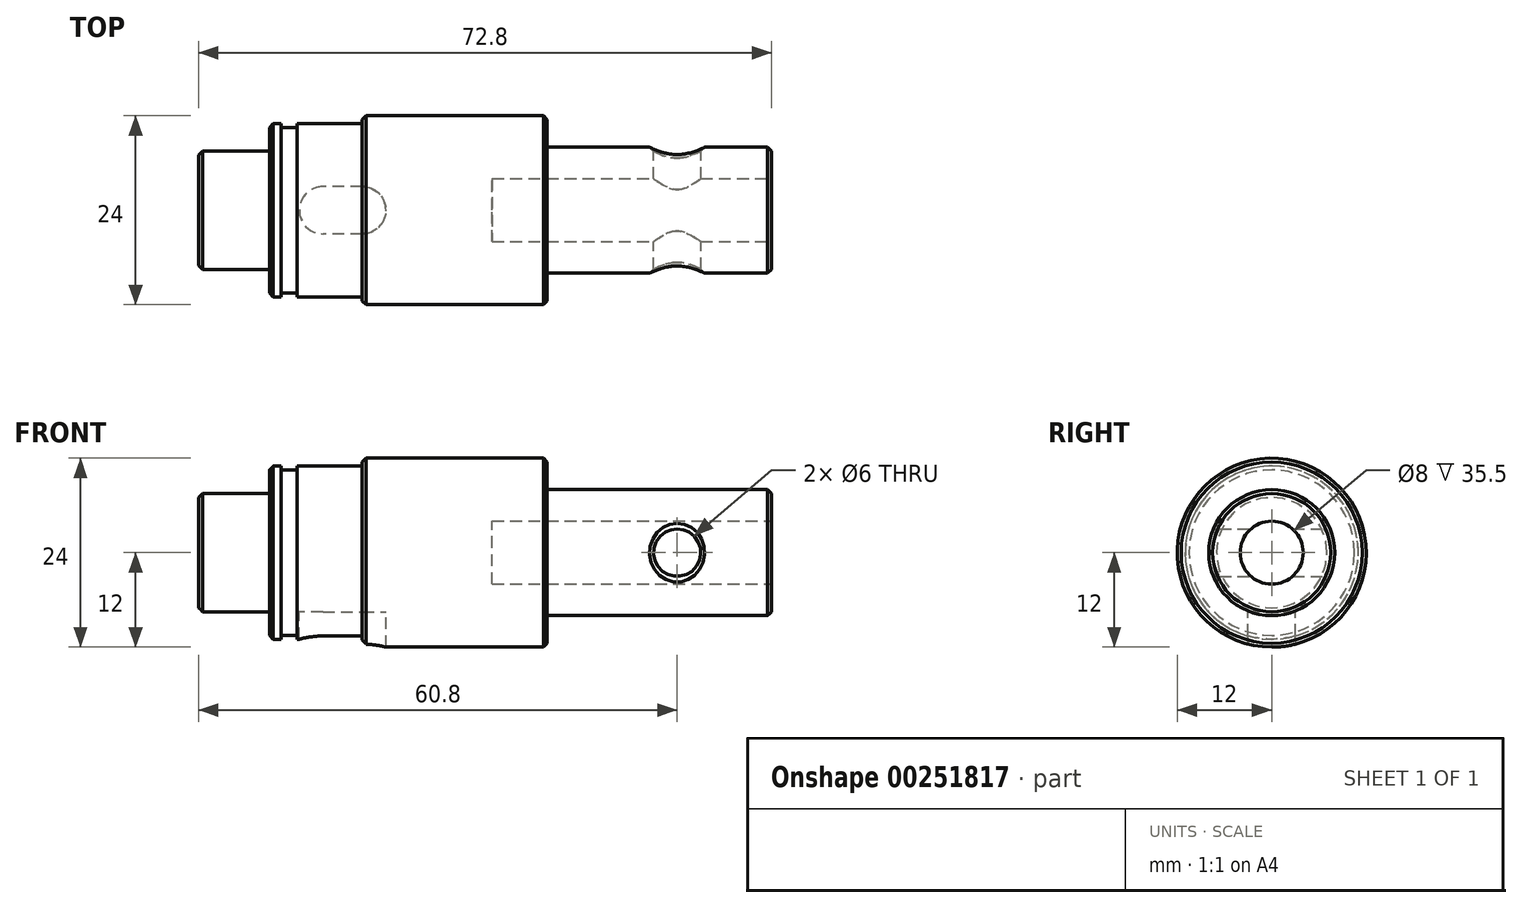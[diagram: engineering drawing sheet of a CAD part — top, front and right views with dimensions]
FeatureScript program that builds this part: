
annotation { "Feature Type Name" : "Feature", "Feature Type Description" : "" }
export const myFeature = defineFeature(function(context is Context, id is Id, definition is map)
    precondition{}
    {
        {
            var Q0;
            Q0=qCreatedBy(makeId("Front.planeOp"),FACE);
            var sketch = newSketch(context, id + "F0", { "sketchPlane" : qUnion([Q0])});
            skLineSegment(sketch, "E0", {"start": v(-50.69, 0) * mm, "end": v(53.02, 0) * mm});
            skLineSegment(sketch, "E1", {"start": v(0, 0) * mm, "end": v(0, 12) * mm});
            skLineSegment(sketch, "E2", {"start": v(0, 12) * mm, "end": v(23.5, 12) * mm});
            skLineSegment(sketch, "E3", {"start": v(23.5, 12) * mm, "end": v(23.5, 0) * mm});
            skLineSegment(sketch, "E4", {"start": v(0, 11) * mm, "end": v(-8.3, 11) * mm});
            skLineSegment(sketch, "E5", {"start": v(-8.3, 11) * mm, "end": v(-8.3, 0) * mm});
            skLineSegment(sketch, "E6", {"start": v(-8.3, 0) * mm, "end": v(0, 0) * mm});
            skLineSegment(sketch, "E7", {"start": v(-8.3, 10.5) * mm, "end": v(-10.3, 10.5) * mm});
            skLineSegment(sketch, "E8", {"start": v(-10.3, 11) * mm, "end": v(-10.3, 0) * mm});
            skLineSegment(sketch, "E9", {"start": v(-10.3, 0) * mm, "end": v(-11.8, 0) * mm});
            skLineSegment(sketch, "E10", {"start": v(-11.8, 0) * mm, "end": v(-11.8, 11) * mm});
            skLineSegment(sketch, "E11", {"start": v(-11.8, 11) * mm, "end": v(-10.3, 11) * mm});
            skLineSegment(sketch, "E12", {"start": v(-11.8, 7.5) * mm, "end": v(-20.8, 7.5) * mm});
            skLineSegment(sketch, "E13", {"start": v(-20.8, 7.5) * mm, "end": v(-20.8, 0) * mm});
            skLineSegment(sketch, "E14", {"start": v(23.5, 8) * mm, "end": v(52, 8) * mm});
            skLineSegment(sketch, "E15", {"start": v(52, 8) * mm, "end": v(52, 0) * mm});
            skSolve(sketch);
        }
        {
            var Q0;
            Q0 = qSketchRegion(id + "F0", true);
            var Q1;
            Q1=sQuery(id+"F0.wireOp",EDGE,"E0");
            revolve(context, id + "F1", {"entities" : qUnion([Q0]), "axis" : qUnion([Q1]), "revolveType" : RevolveType.FULL});
        }
        {
            var Q0;
            Q0=qCreatedBy(makeId("Top.planeOp"),FACE);
            cPlane(context, id + "F2", {"entities" : qUnion([Q0]), "cplaneType" : CPlaneType.OFFSET, "offset" : 7.5 * mm, "oppositeDirection" : true, "width" : 150 * mm, "height" : 150 * mm});
        }
        {
            var Q0;
            Q0=qCreatedBy(id+"F2.planeOp",FACE);
            var sketch = newSketch(context, id + "F3", { "sketchPlane" : qUnion([Q0])});
            skArc(sketch, "E16", {"start": v(0, -3) * mm, "mid": v(3, 0) * mm, "end": v(0, 3) * mm});
            skArc(sketch, "E17", {"start": v(-5, 3) * mm, "mid": v(-8, 0) * mm, "end": v(-5, -3) * mm});
            skLineSegment(sketch, "E18", {"start": v(-5, -2.48) * mm, "end": v(-5, 2.81) * mm, "construction": true});
            skLineSegment(sketch, "E19", {"start": v(0, -2.85) * mm, "end": v(0, 3.74) * mm, "construction": true});
            skLineSegment(sketch, "E20", {"start": v(-5, -3) * mm, "end": v(0, -3) * mm});
            skLineSegment(sketch, "E21", {"start": v(-5, 3) * mm, "end": v(0, 3) * mm});
            skSolve(sketch);
        }
        {
            var Q0;
            Q0 = qSketchRegion(id + "F3", true);
            extrude(context, id + "F4", {"entities" : qUnion([Q0]), "operationType" : NewBodyOperationType.REMOVE, "endBound" : BoundingType.THROUGH_ALL, "oppositeDirection" : true, "depth" : 25 * mm});
        }
        {
            var Q0;
            Q0=qCreatedBy(makeId("Front.planeOp"),FACE);
            var sketch = newSketch(context, id + "F5", { "sketchPlane" : qUnion([Q0])});
            skCircle(sketch, "E22", {"center": v(40, 0) * mm, "radius": 3 * mm});
            skSolve(sketch);
        }
        {
            var Q0;
            Q0 = qSketchRegion(id + "F5", true);
            extrude(context, id + "F6", {"entities" : qUnion([Q0]), "operationType" : NewBodyOperationType.REMOVE, "endBound" : BoundingType.SYMMETRIC, "depth" : 25 * mm});
        }
        {
            var Q0;
            Q0=makeQuery(id+"F1.opRevolve","SWEPT_FACE",FACE,{"disambiguationData":[OSD([sQuery(id+"F0.wireOp",EDGE,"E15")])]});
            var sketch = newSketch(context, id + "F7", { "sketchPlane" : qUnion([Q0])});
            skCircle(sketch, "E23", {"center": v(0, 0) * mm, "radius": 4 * mm});
            skSolve(sketch);
        }
        {
            var Q0;
            Q0=makeQuery(id+"F7.imprint","IMPRINT",FACE,{"disambiguationData":[TD([[makeQuery(id+"F7.imprint","IMPRINT",EDGE,{"derivedFrom":sQuery(id+"F7.wireOp",EDGE,"E23")}),1.0]])]});
            extrude(context, id + "F8", {"entities" : qUnion([Q0]), "operationType" : NewBodyOperationType.REMOVE, "oppositeDirection" : true, "depth" : 35.5 * mm});
        }
        {
            var Q0;
            Q0=makeQuery(id+"F1.opRevolve","SWEPT_EDGE",EDGE,{"disambiguationData":[OSD([sQuery(id+"F0.wireOp",EDGE,"E12"),sQuery(id+"F0.wireOp",EDGE,"E13")])]});
            var Q1;
            Q1=makeQuery(id+"F1.opRevolve","SWEPT_EDGE",EDGE,{"disambiguationData":[OSD([sQuery(id+"F0.wireOp",EDGE,"E10"),sQuery(id+"F0.wireOp",EDGE,"E11")])]});
            var Q2;
            Q2=makeQuery(id+"F1.opRevolve","SWEPT_EDGE",EDGE,{"disambiguationData":[OSD([sQuery(id+"F0.wireOp",EDGE,"E1"),sQuery(id+"F0.wireOp",EDGE,"E2")])]});
            var Q3;
            Q3=makeQuery(id+"F1.opRevolve","SWEPT_EDGE",EDGE,{"disambiguationData":[OSD([sQuery(id+"F0.wireOp",EDGE,"E2"),sQuery(id+"F0.wireOp",EDGE,"E3")])]});
            var Q4;
            Q4=makeQuery(id+"F1.opRevolve","SWEPT_EDGE",EDGE,{"disambiguationData":[OSD([sQuery(id+"F0.wireOp",EDGE,"E14"),sQuery(id+"F0.wireOp",EDGE,"E15")])]});
            var Q5;
            Q5=makeQuery(id+"F8.boolean.opBoolean","COPY",EDGE,{"derivedFrom":makeQuery(id+"F8.opExtrude","CAP_EDGE",EDGE,{"disambiguationData":[OSD([sQuery(id+"F7.wireOp",EDGE,"E23")])],"isStart":true})});
            var Q6;
            Q6=makeQuery(id+"F6.boolean.opBoolean","INTERSECT",EDGE,{"disambiguationData":[OD(0.0)],"derivedFrom":[makeQuery(id+"F1.opRevolve","SWEPT_FACE",FACE,{"disambiguationData":[OSD([sQuery(id+"F0.wireOp",EDGE,"E14")])]}),makeQuery(id+"F6.opExtrude","SWEPT_FACE",FACE,{"disambiguationData":[OSD([sQuery(id+"F5.wireOp",EDGE,"E22")])]})]});
            var Q7;
            Q7=makeQuery(id+"F6.boolean.opBoolean","INTERSECT",EDGE,{"disambiguationData":[OD(1.0)],"derivedFrom":[makeQuery(id+"F1.opRevolve","SWEPT_FACE",FACE,{"disambiguationData":[OSD([sQuery(id+"F0.wireOp",EDGE,"E14")])]}),makeQuery(id+"F6.opExtrude","SWEPT_FACE",FACE,{"disambiguationData":[OSD([sQuery(id+"F5.wireOp",EDGE,"E22")])]})]});
            chamfer(context, id + "F9", {"entities" : qUnion([Q0, Q1, Q2, Q3, Q4, Q5, Q6, Q7]), "width" : .5 * mm, "tangentPropagation" : true});
        }
    });
